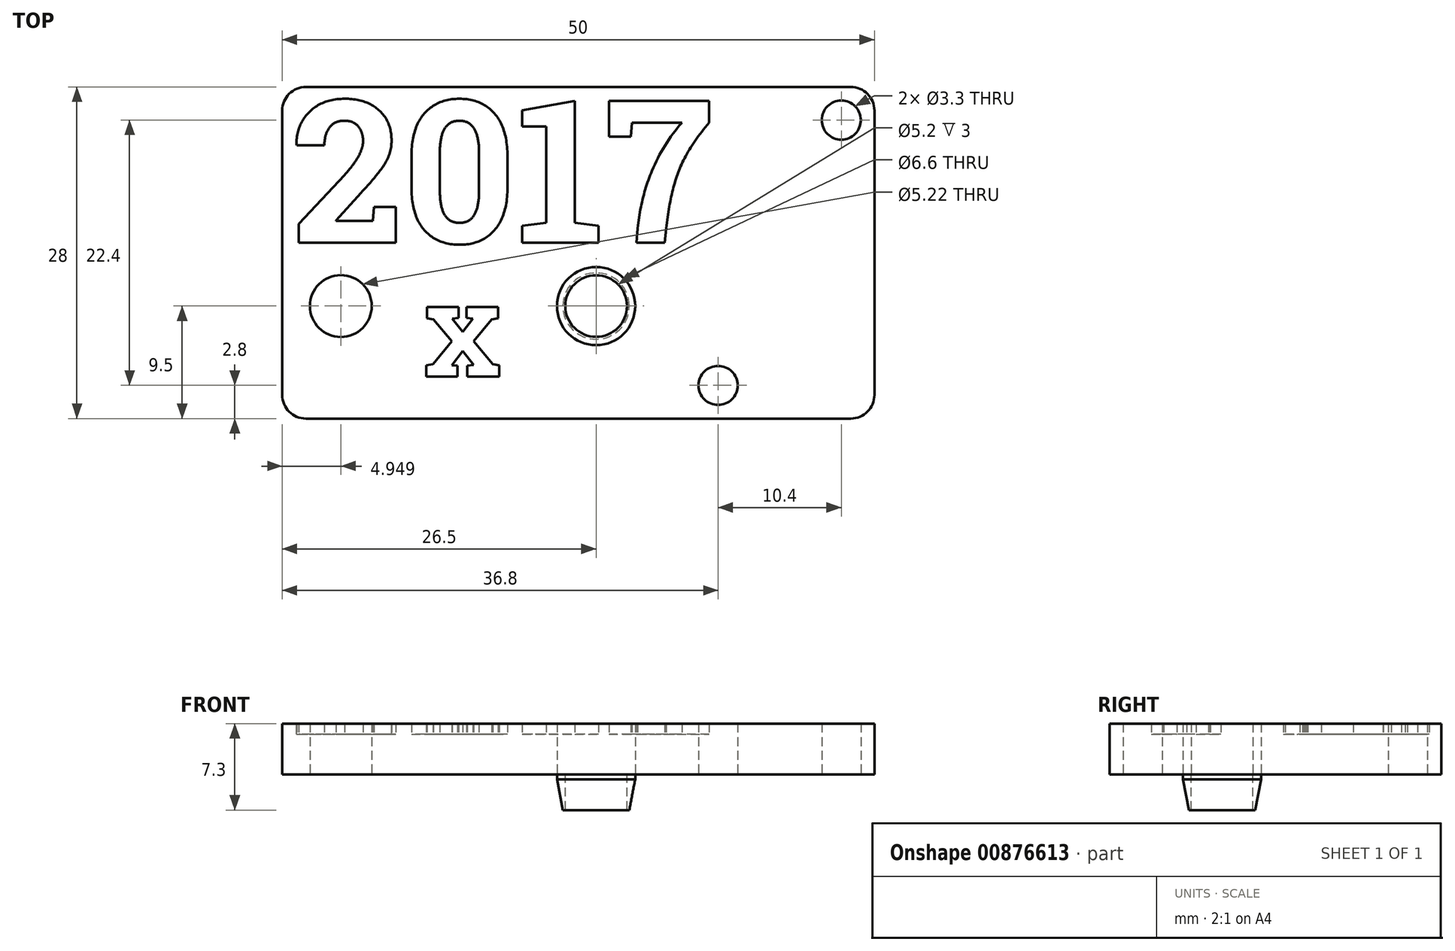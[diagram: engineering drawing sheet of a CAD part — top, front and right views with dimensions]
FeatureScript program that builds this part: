
annotation { "Feature Type Name" : "Feature", "Feature Type Description" : "" }
export const myFeature = defineFeature(function(context is Context, id is Id, definition is map)
    precondition{}
    {
        {
            var Q0;
            Q0=qCreatedBy(makeId("Top.planeOp"),FACE);
            var sketch = newSketch(context, id + "F0", { "sketchPlane" : qUnion([Q0])});
            skLineSegment(sketch, "E0.bottom", {"start": v(0, 0) * mm, "end": v(-50, 0) * mm});
            skLineSegment(sketch, "E0.top", {"start": v(0, 28) * mm, "end": v(-50, 28) * mm});
            skLineSegment(sketch, "E0.left", {"start": v(0, 0) * mm, "end": v(0, 28) * mm});
            skLineSegment(sketch, "E0.right", {"start": v(-50, 0) * mm, "end": v(-50, 28) * mm});
            skLineSegment(sketch, "E1", {"start": v(-16, 28) * mm, "end": v(-16, 0) * mm, "construction": true});
            skCircle(sketch, "E2", {"center": v(-23.5, 9.5) * mm, "radius": 2.6 * mm});
            skCircle(sketch, "E3", {"center": v(-23.5, 9.5) * mm, "radius": 3.3 * mm});
            skCircle(sketch, "E4", {"center": v(-13.2, 2.8) * mm, "radius": 1.65 * mm});
            skCircle(sketch, "E5", {"center": v(-2.8, 25.2) * mm, "radius": 1.65 * mm});
            skCircle(sketch, "E6", {"center": v(-45.05, 9.5) * mm, "radius": 2.61 * mm});
            skSolve(sketch);
        }
        {
            var Q0;
            Q0=makeQuery(id+"F0.imprint","IMPRINT",FACE,{"disambiguationData":[TD([[makeQuery(id+"F0.imprint","IMPRINT",EDGE,{"derivedFrom":sQuery(id+"F0.wireOp",EDGE,"E0.bottom")}),-1.0]])]});
            extrude(context, id + "F1", {"entities" : qUnion([Q0]), "depth" : 4.3 * mm, "offsetDistance" : 25 * mm});
        }
        {
            var Q0;
            Q0=makeQuery(id+"F0.imprint","IMPRINT",FACE,{"disambiguationData":[TD([[makeQuery(id+"F0.imprint","IMPRINT",EDGE,{"derivedFrom":sQuery(id+"F0.wireOp",EDGE,"E2")}),-1.0]])]});
            extrude(context, id + "F2", {"entities" : qUnion([Q0]), "operationType" : NewBodyOperationType.ADD, "oppositeDirection" : true, "depth" : 3 * mm, "offsetDistance" : 25 * mm});
        }
        {
            var Q0;
            Q0=makeQuery(id+"F2.opExtrude","CAP_EDGE",EDGE,{"disambiguationData":[OSD([sQuery(id+"F0.wireOp",EDGE,"E3")])],"isStart":false});
            chamfer(context, id + "F3", {"entities" : qUnion([Q0]), "chamferType" : ChamferType.TWO_OFFSETS, "width1" : 0.5 * mm, "oppositeDirection" : true, "width2" : 2.6 * mm});
        }
        {
            var Q0;
            Q0=makeQuery(id+"F1.opExtrude","SWEPT_EDGE",EDGE,{"disambiguationData":[OSD([sQuery(id+"F0.wireOp",EDGE,"E0.top"),sQuery(id+"F0.wireOp",EDGE,"E0.left")])]});
            var Q1;
            Q1=makeQuery(id+"F1.opExtrude","SWEPT_EDGE",EDGE,{"disambiguationData":[OSD([sQuery(id+"F0.wireOp",EDGE,"E0.top"),sQuery(id+"F0.wireOp",EDGE,"E0.right")])]});
            var Q2;
            Q2=makeQuery(id+"F1.opExtrude","SWEPT_EDGE",EDGE,{"disambiguationData":[OSD([sQuery(id+"F0.wireOp",EDGE,"E0.bottom"),sQuery(id+"F0.wireOp",EDGE,"E0.right")])]});
            var Q3;
            Q3=makeQuery(id+"F1.opExtrude","SWEPT_EDGE",EDGE,{"disambiguationData":[OSD([sQuery(id+"F0.wireOp",EDGE,"E0.bottom"),sQuery(id+"F0.wireOp",EDGE,"E0.left")])]});
            fillet(context, id + "F4", {"entities" : qUnion([Q0, Q1, Q2, Q3]), "radius" : 2 * mm, "tangentPropagation" : true, "allowEdgeOverflow" : false});
        }
        {
            var Q0;
            Q0=qCreatedBy(makeId("Top.planeOp"),FACE);
            var sketch = newSketch(context, id + "F5", { "sketchPlane" : qUnion([Q0])});
            skText(sketch, "E7", { "text": "2017", "fontName": "RobotoSlab-Bold.ttf"});
            skText(sketch, "E8", { "text": "x", "fontName": "RobotoSlab-Bold.ttf"});
            const initialGuessF5  = {"E7": [-0.0492, 0.01485, 1, 0, 0.01213], "E8": [-0.038, 0.00354, 1, 0, 0.00802]};
            skSetInitialGuess(sketch, initialGuessF5);
            skSolve(sketch);
        }
        {
            var Q0;
            Q0=makeQuery(id+"F5.imprint","IMPRINT",FACE,{"disambiguationData":[TD([[makeQuery(id+"F5.imprint","IMPRINT",EDGE,{"derivedFrom":sQuery(id+"F5.wireOp",EDGE,"E7.sketch_text.stroke-53")}),-1.0]])]});
            var Q1;
            Q1=makeQuery(id+"F5.imprint","IMPRINT",FACE,{"disambiguationData":[TD([[makeQuery(id+"F5.imprint","IMPRINT",EDGE,{"derivedFrom":sQuery(id+"F5.wireOp",EDGE,"E7.sketch_text.stroke-43")}),-1.0]])]});
            var Q2;
            Q2=makeQuery(id+"F5.imprint","IMPRINT",FACE,{"disambiguationData":[TD([[makeQuery(id+"F5.imprint","IMPRINT",EDGE,{"derivedFrom":sQuery(id+"F5.wireOp",EDGE,"E7.sketch_text.stroke-23")}),-1.0]])]});
            var Q3;
            Q3=makeQuery(id+"F5.imprint","IMPRINT",FACE,{"disambiguationData":[TD([[makeQuery(id+"F5.imprint","IMPRINT",EDGE,{"derivedFrom":sQuery(id+"F5.wireOp",EDGE,"E7.sketch_text.stroke-0")}),-1.0]])]});
            var Q4;
            Q4=makeQuery(id+"F5.imprint","IMPRINT",FACE,{"disambiguationData":[TD([[makeQuery(id+"F5.imprint","IMPRINT",EDGE,{"derivedFrom":sQuery(id+"F5.wireOp",EDGE,"E8.sketch_text.stroke-0")}),-1.0]])]});
            extrude(context, id + "F6", {"entities" : qUnion([Q0, Q1, Q2, Q3, Q4]), "operationType" : NewBodyOperationType.REMOVE, "depth" : 25 * mm, "offsetDistance" : 25 * mm, "hasSecondDirection" : true, "secondDirectionOppositeDirection" : false, "secondDirectionDepth" : 3.4 * mm});
        }
    });
